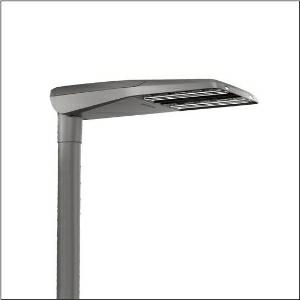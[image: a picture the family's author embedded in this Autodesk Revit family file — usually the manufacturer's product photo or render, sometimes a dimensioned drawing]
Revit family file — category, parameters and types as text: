
# Revit family: streetlight_sl_11_iq_midi___st1_2a_5xc3a41f08me_055e
name_source: partatom
category: Lighting Fixtures
units: mm (PartAtom-declared; Revit-internal decimal feet)

## family parameters
Cut with Voids When Loaded = No
Host = Face
Light Source = No
Part Type = Normal
Room Calculation Point = No
Round Connector Dimension = Use Diameter
Shared = No

## types (1)
- --- (1 x LED, 18900 lm, 124.7 W, 4000K)
    Apparent Load = 125 VA
    CIE Flux Codes = 32 70 96 100 100
    Color Rendering = 70
    Color Temperature = 4000K
    Default Elevation = 1800 mm
    Description = Streetlight SL 11 iQ midi, mast luminaire, primary light control with 3 zone facetted reflector, of plastic, silver coated, highly specular, primary optical cover: cover, of PMMA, transparent, light distribution: ST1.2a, light emission: direct distribution, primary light characteristic: asymmetric, installation type: post-top, side-entry, lamps: LED, High Power LED, rated values: 18.900lm | 124,7W | 151,6lm/W (begin service life); end service life: 18.900lm | 132,2W; at 50% lumin. flux: 9.450lm | 57,4W | 164,6lm/W, colour temperature: 4000K, colour rendering: CRI > 70, light colour: 740, light setting 1 begin service life: 100% | 18.900lm | 124,7W | 151,6lm/W | 4.000K, light setting 1 end service life: 132,2W, further light settings possible, control: Street-Remote, optimised constant luminous flux control (CLO 2.0), Desk-Remote (wireless, voltage-free reading and setting of iQ features in the workshop via application-optimized NFC function/RFID function), Light-Fading, Smart-Wire, Night-Set, Lumen-Switch, Temp-Guard, Auto-Match, with cable H07RN-F 5x 1.5mm², mains connection: 230..240V, AC, 50/60Hz, connection cable pre-assembled, cable length: 12,5m, luminaire housing, of diecast aluminium, powder-coated, Siteco® metallic grey (DB 702S), please order mast flange separately, inclination adjustable without tools: 0°, 5°, 10°, 15° (post-top) | 0°, -5°, -10°, -15° (side-entry), sealing non-destructively replaceable, multi-level sealing system, length: 780mm, width: 376mm, height: 118mm, mast flange for spigot size: 42mm (side-entry): 5XC10008XM4, 60/48mm (side-entry/post-top): 5XC10108XM2, 76/60mm (side-entry/post-top): 5XC10108XM1, equipment: Power, protection rating (complete): IP66, insulation class (complete): insulation class II (safety insulation), certification: CE, ENEC, ENEC+, VDE, impact resistance: IK10, permissible operating ambient temperature for outdoor applications: -25..+50°C, standard-compliant lighting for roads and squares, Environmental Product Declaration (EPD) tested and certified by an independent institute, packaging unit: 1 piece

Light Distribution: ST1.2a
    Height = 118 mm
    Lamp = 1 x LED
    Lamp Light Flux = 18900 lm
    Lamp Power = 124.7 W
    Lamp count = 1
    Length = 780 mm
    Luminous efficacy = 152 lm/W
    Manufacturer = Siteco
    ModVariant = No
    Model = 5XC3A41F08ME
    Number of Poles = 1
    OnlyDefault = Yes
    Power Factor = 1
    Product Name = Streetlight SL 11 iQ midi | ST1.2a
    Product group = mast luminaire | pylon top
    ProductGroupID = 6100
    Protection Class = Protection class II
    Protection Degree = IP 66
    RLX_Detail_Level = 1
    RLX_Emergency_Light_Flux = 0 lm
    RLX_Emergency_Type = 0
    RLX_Emergency_Type_DB = No
    RlxData = <blob elided: 71041 chars, md5=0612e846>
    Socket = socket
    Standby Power = 0 W
    System Light Flux = 18900 lm
    System Power = 125 W
    Type Comments = factory setting: luminous flux: 100 % | dim-lin: 254 | 557 mA
    Type Image = l_1005960.jpg
    URL = http://relux.com
    VarID = @adj_217597
    Voltage = 0 V
    Weight = 0.00 kg
    Width = 376 mm

## geometry (parser evidence)
native form markers: Blend x4, Sweep x9
no freeform markers — native parametric forms only
